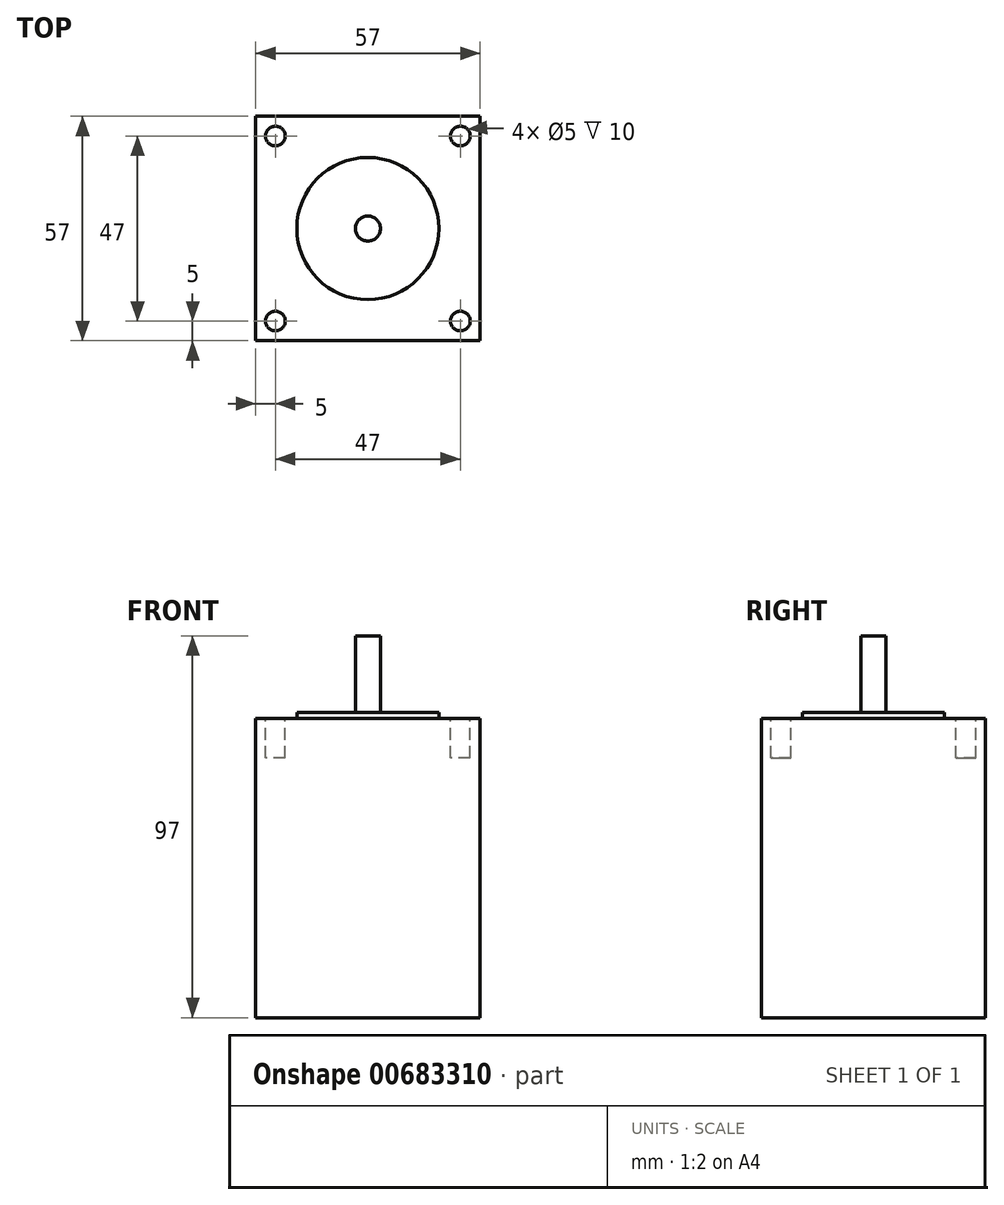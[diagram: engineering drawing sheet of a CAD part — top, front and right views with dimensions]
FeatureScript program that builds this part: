
annotation { "Feature Type Name" : "Feature", "Feature Type Description" : "" }
export const myFeature = defineFeature(function(context is Context, id is Id, definition is map)
    precondition{}
    {
        {
            var Q0;
            Q0=qCreatedBy(makeId("Top.planeOp"),FACE);
            var sketch = newSketch(context, id + "F0", { "sketchPlane" : qUnion([Q0])});
            skLineSegment(sketch, "E0.bottom", {"start": v(28.5, 28.5) * mm, "end": v(-28.5, 28.5) * mm});
            skLineSegment(sketch, "E0.top", {"start": v(28.5, -28.5) * mm, "end": v(-28.5, -28.5) * mm});
            skLineSegment(sketch, "E0.left", {"start": v(28.5, 28.5) * mm, "end": v(28.5, -28.5) * mm});
            skLineSegment(sketch, "E0.right", {"start": v(-28.5, 28.5) * mm, "end": v(-28.5, -28.5) * mm});
            skPoint(sketch, "E0.middle", {"position": v(0, 0) * mm});
            skSolve(sketch);
        }
        {
            var Q0;
            Q0 = qSketchRegion(id + "F0", true);
            extrude(context, id + "F1", {"entities" : qUnion([Q0]), "depth" : 76 * mm, "offsetDistance" : 25 * mm});
        }
        {
            var Q0;
            Q0=makeQuery(id+"F1.opExtrude","CAP_FACE",FACE,{"disambiguationData":[OSD([sQuery(id+"F0.wireOp",EDGE,"E0.bottom"),sQuery(id+"F0.wireOp",EDGE,"E0.top"),sQuery(id+"F0.wireOp",EDGE,"E0.left"),sQuery(id+"F0.wireOp",EDGE,"E0.right")])],"isStart":false});
            var sketch = newSketch(context, id + "F2", { "sketchPlane" : qUnion([Q0])});
            skCircle(sketch, "E1", {"center": v(0, 0) * mm, "radius": 18.05 * mm});
            skCircle(sketch, "E2", {"center": v(0, 0) * mm, "radius": 3.17 * mm});
            skSolve(sketch);
        }
        {
            var Q0;
            Q0 = qSketchRegion(id + "F2", true);
            extrude(context, id + "F3", {"entities" : qUnion([Q0]), "operationType" : NewBodyOperationType.ADD, "depth" : 1.6 * mm, "offsetDistance" : 25 * mm});
        }
        {
            var Q0;
            Q0=makeQuery(id+"F2.imprint","IMPRINT",FACE,{"disambiguationData":[TD([[makeQuery(id+"F2.imprint","IMPRINT",EDGE,{"derivedFrom":sQuery(id+"F2.wireOp",EDGE,"E2")}),1.0]])]});
            extrude(context, id + "F4", {"entities" : qUnion([Q0]), "operationType" : NewBodyOperationType.ADD, "depth" : 21 * mm, "offsetDistance" : 25 * mm});
        }
        {
            var Q0;
            Q0=makeQuery(id+"F2.imprint","IMPRINT",FACE,{"disambiguationData":[TD([[makeQuery(id+"F2.imprint","IMPRINT",EDGE,{"derivedFrom":sQuery(id+"F2.wireOp",EDGE,"E1")}),-1.0]])]});
            var sketch = newSketch(context, id + "F5", { "sketchPlane" : qUnion([Q0])});
            skLineSegment(sketch, "E3.bottom", {"start": v(23.5, -23.5) * mm, "end": v(-23.5, -23.5) * mm, "construction": true});
            skLineSegment(sketch, "E3.top", {"start": v(23.5, 23.5) * mm, "end": v(-23.5, 23.5) * mm, "construction": true});
            skLineSegment(sketch, "E3.left", {"start": v(23.5, -23.5) * mm, "end": v(23.5, 23.5) * mm, "construction": true});
            skLineSegment(sketch, "E3.right", {"start": v(-23.5, -23.5) * mm, "end": v(-23.5, 23.5) * mm, "construction": true});
            skPoint(sketch, "E3.middle", {"position": v(0, 0) * mm});
            skCircle(sketch, "E4", {"center": v(-23.5, 23.5) * mm, "radius": 2.5 * mm});
            skCircle(sketch, "E5", {"center": v(23.5, 23.5) * mm, "radius": 2.5 * mm});
            skCircle(sketch, "E6", {"center": v(23.5, -23.5) * mm, "radius": 2.5 * mm});
            skCircle(sketch, "E7", {"center": v(-23.5, -23.5) * mm, "radius": 2.5 * mm});
            skSolve(sketch);
        }
        {
            var Q0;
            Q0 = qSketchRegion(id + "F5", true);
            extrude(context, id + "F6", {"entities" : qUnion([Q0]), "operationType" : NewBodyOperationType.REMOVE, "oppositeDirection" : true, "depth" : 10 * mm, "offsetDistance" : 25 * mm});
        }
    });
